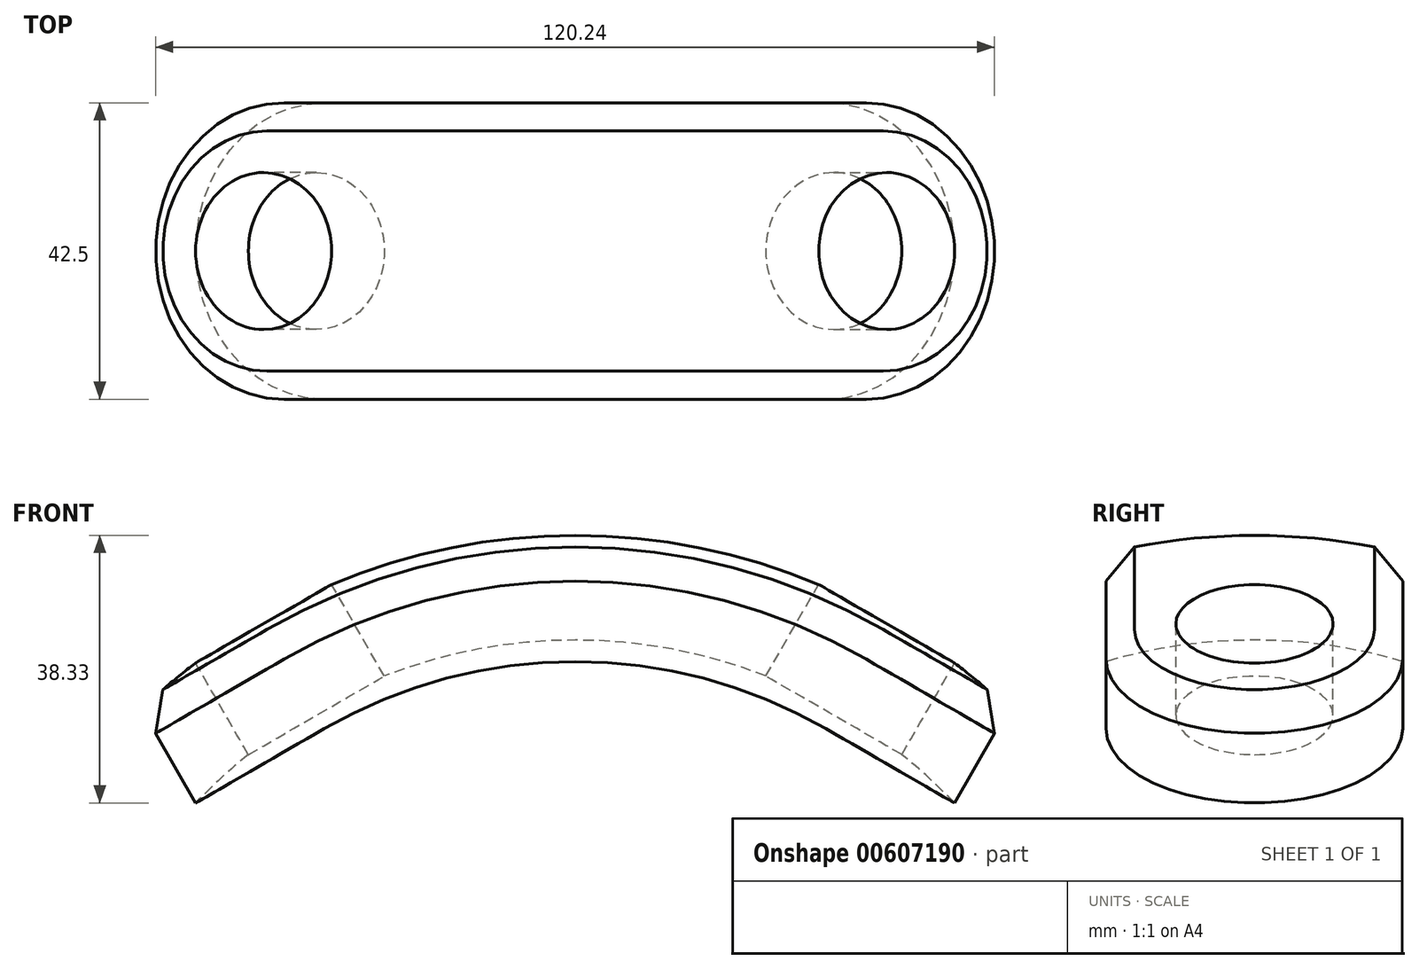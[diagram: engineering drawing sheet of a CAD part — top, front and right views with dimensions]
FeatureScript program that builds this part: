
annotation { "Feature Type Name" : "Feature", "Feature Type Description" : "" }
export const myFeature = defineFeature(function(context is Context, id is Id, definition is map)
    precondition{}
    {
        {
            var Q0;
            Q0=qCreatedBy(makeId("Front.planeOp"),FACE);
            var sketch = newSketch(context, id + "F0", { "sketchPlane" : qUnion([Q0])});
            skLineSegment(sketch, "E0", {"start": v(0, 0) * mm, "end": v(-62.13, 107.61) * mm, "construction": true});
            skLineSegment(sketch, "E1", {"start": v(0, 42.5) * mm, "end": v(-62.13, 107.61) * mm, "construction": true});
            skCircle(sketch, "E2", {"center": v(0, 42.5) * mm, "radius": 90 * mm, "construction": true});
            skCircle(sketch, "E3", {"center": v(0, 42.5) * mm, "radius": 75 * mm, "construction": true});
            skLineSegment(sketch, "E4", {"start": v(0, 42.5) * mm, "end": v(-37.5, 107.45) * mm, "construction": true});
            skArc(sketch, "E5", {"start": v(-62.13, 107.61) * mm, "mid": v(-33.46, 126.05) * mm, "end": v(0, 132.5) * mm});
            skArc(sketch, "E6", {"start": v(-51.75, 89.64) * mm, "mid": v(-28.29, 106.53) * mm, "end": v(0, 112.5) * mm});
            skLineSegment(sketch, "E7", {"start": v(0, 112.5) * mm, "end": v(0, 132.5) * mm});
            skLineSegment(sketch, "E8", {"start": v(-51.75, 89.64) * mm, "end": v(-62.13, 107.61) * mm});
            skPoint(sketch, "E9", {"position": v(0, 0) * mm});
            skPoint(sketch, "E10", {"position": v(-45, 120.44) * mm});
            skLineSegment(sketch, "E11", {"start": v(-70.96, 105.45) * mm, "end": v(-27.16, 130.74) * mm, "construction": true});
            skSolve(sketch);
        }
        {
            var Q0;
            Q0 = qSketchRegion(id + "F0", true);
            extrude(context, id + "F1", {"entities" : qUnion([Q0]), "endBound" : BoundingType.SYMMETRIC, "depth" : 42.5 * mm, "offsetDistance" : 25 * mm});
        }
        {
            var Q0;
            Q0=qCreatedBy(makeId("Right.planeOp"),FACE);
            var sketch = newSketch(context, id + "F2", { "sketchPlane" : qUnion([Q0])});
            skLineSegment(sketch, "E12", {"start": v(-25, 42.5) * mm, "end": v(25, 42.5) * mm, "construction": true});
            skArc(sketch, "E13", {"start": v(25, 128.96) * mm, "mid": v(0, 132.5) * mm, "end": v(-25, 128.96) * mm});
            skLineSegment(sketch, "E14.bottom", {"start": v(-25, 148.96) * mm, "end": v(25, 148.96) * mm});
            skLineSegment(sketch, "E14.left", {"start": v(-25, 148.96) * mm, "end": v(-25, 128.96) * mm});
            skLineSegment(sketch, "E14.right", {"start": v(25, 148.96) * mm, "end": v(25, 128.96) * mm});
            skSolve(sketch);
        }
        {
            var Q0;
            Q0 = qSketchRegion(id + "F2", true);
            var Q1;
            Q1=sQuery(id+"F2.wireOp",EDGE,"E12");
            revolve(context, id + "F3", {"operationType" : NewBodyOperationType.REMOVE, "entities" : qUnion([Q0]), "axis" : qUnion([Q1]), "revolveType" : RevolveType.FULL, "oppositeDirection" : true});
        }
        {
            var Q0;
            Q0=qCreatedBy(makeId("Right.planeOp"),FACE);
            var sketch = newSketch(context, id + "F4", { "sketchPlane" : qUnion([Q0])});
            skLineSegment(sketch, "E15", {"start": v(-25, 42.5) * mm, "end": v(25, 42.5) * mm, "construction": true});
            skArc(sketch, "E16", {"start": v(25, 113.21) * mm, "mid": v(0, 117.5) * mm, "end": v(-25, 113.21) * mm});
            skLineSegment(sketch, "E17.top", {"start": v(-25, 83.21) * mm, "end": v(25, 83.21) * mm});
            skLineSegment(sketch, "E17.left", {"start": v(-25, 113.21) * mm, "end": v(-25, 83.21) * mm});
            skLineSegment(sketch, "E17.right", {"start": v(25, 113.21) * mm, "end": v(25, 83.21) * mm});
            skSolve(sketch);
        }
        {
            var Q0;
            Q0 = qSketchRegion(id + "F4", true);
            var Q1;
            Q1=sQuery(id+"F4.wireOp",EDGE,"E15");
            revolve(context, id + "F5", {"operationType" : NewBodyOperationType.REMOVE, "entities" : qUnion([Q0]), "axis" : qUnion([Q1]), "revolveType" : RevolveType.FULL, "oppositeDirection" : true});
        }
        {
            var Q0;
            Q0=makeQuery(id+"F1.opExtrude","CAP_EDGE",EDGE,{"disambiguationData":[OSD([sQuery(id+"F0.wireOp",EDGE,"E8")])],"isStart":true});
            var Q1;
            Q1=makeQuery(id+"F1.opExtrude","CAP_EDGE",EDGE,{"disambiguationData":[OSD([sQuery(id+"F0.wireOp",EDGE,"E8")])],"isStart":false});
            fillet(context, id + "F6", {"entities" : qUnion([Q0, Q1]), "radius" : 21.25 * mm, "tangentPropagation" : true, "allowEdgeOverflow" : false});
        }
        {
            var Q0;
            Q0=sQuery(id+"F0.wireOp",EDGE,"E11");
            cPlane(context, id + "F7", {"entities" : qUnion([Q0]), "cplaneType" : CPlaneType.LINE_ANGLE, "offset" : 25 * mm, "angle" : 90 * degree, "width" : 150 * mm, "height" : 150 * mm});
        }
        {
            var Q0;
            Q0=qCreatedBy(id+"F7.planeOp",FACE);
            var sketch = newSketch(context, id + "F8", { "sketchPlane" : qUnion([Q0])});
            skPoint(sketch, "E18", {"position": v(21.25, 0) * mm});
            skSolve(sketch);
        }
        {
            var Q0;
            Q0=sQuery(id+"F8.wireOp",VERTEX,"E18");
            var Q1;
            Q1=makeQuery(id+"F1.opExtrude","SWEPT_BODY",BODY,{"disambiguationData":[OSD([sQuery(id+"F0.wireOp",EDGE,"E5"),sQuery(id+"F0.wireOp",EDGE,"E6"),sQuery(id+"F0.wireOp",EDGE,"E7"),sQuery(id+"F0.wireOp",EDGE,"E8")])]});
            hole(context, id + "F9", {"style" : HoleStyle.SIMPLE, "endStyle" : HoleEndStyle.THROUGH, "holeDiameter" : 22.5 * mm, "majorDiameter" : 5 * mm, "isTappedThrough" : true, "tappedDepth" : 12 * mm, "tapClearance" : 3, "startFromSketch" : true, "locations" : qUnion([Q0]), "scope" : qUnion([Q1])});
        }
        {
            var Q0;
            Q0=makeQuery(id+"F1.opExtrude","SWEPT_BODY",BODY,{"disambiguationData":[OSD([sQuery(id+"F0.wireOp",EDGE,"E5"),sQuery(id+"F0.wireOp",EDGE,"E6"),sQuery(id+"F0.wireOp",EDGE,"E7"),sQuery(id+"F0.wireOp",EDGE,"E8")])]});
            var Q1;
            Q1=qCreatedBy(makeId("Right.planeOp"),FACE);
            mirror(context, id + "F10", {"operationType" : NewBodyOperationType.ADD, "entities" : qUnion([Q0]), "mirrorPlane" : qUnion([Q1])});
        }
        {
            var Q0;
            {var subQ0=makeQuery(id+"F3.boolean.opBoolean","INTERSECT",EDGE,{"derivedFrom":[makeQuery(id+"F1.opExtrude","CAP_FACE",FACE,{"disambiguationData":[OSD([sQuery(id+"F0.wireOp",EDGE,"E5"),sQuery(id+"F0.wireOp",EDGE,"E6"),sQuery(id+"F0.wireOp",EDGE,"E7"),sQuery(id+"F0.wireOp",EDGE,"E8")])],"isStart":false}),makeQuery(id+"F3.opRevolve","SWEPT_FACE",FACE,{"disambiguationData":[OSD([sQuery(id+"F2.wireOp",EDGE,"E13")])]})]});Q0=makeQuery(id+"F10.boolean.opBoolean","MERGE",EDGE,{"derivedFrom":[subQ0,makeQuery(id+"F10.opPattern","COPY",EDGE,{"derivedFrom":subQ0,"instanceName":"1"})]});}
            chamfer(context, id + "F11", {"entities" : qUnion([Q0]), "width" : 5 * mm, "tangentPropagation" : true});
        }
    });
